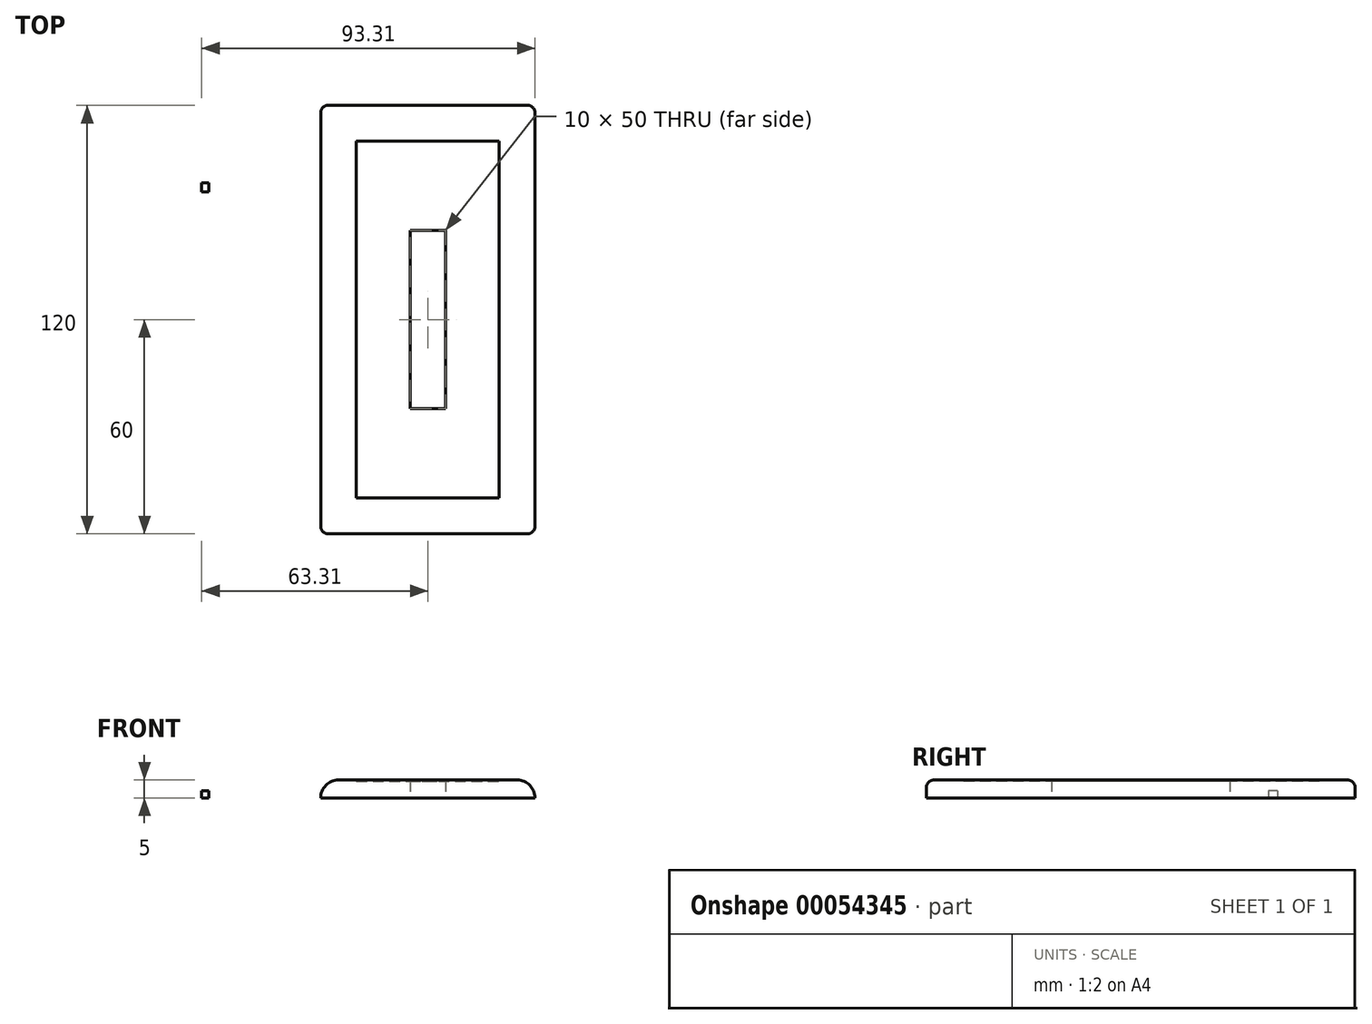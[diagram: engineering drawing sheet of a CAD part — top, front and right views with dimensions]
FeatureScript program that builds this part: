
annotation { "Feature Type Name" : "Feature", "Feature Type Description" : "" }
export const myFeature = defineFeature(function(context is Context, id is Id, definition is map)
    precondition{}
    {
        {
            var Q0;
            Q0=qCreatedBy(makeId("Top.planeOp"),FACE);
            var sketch = newSketch(context, id + "F0", { "sketchPlane" : qUnion([Q0])});
            skLineSegment(sketch, "E0.rect.bottom", {"start": v(-30, 60) * mm, "end": v(30, 60) * mm});
            skLineSegment(sketch, "E0.rect.top", {"start": v(-30, -60) * mm, "end": v(30, -60) * mm});
            skLineSegment(sketch, "E0.rect.left", {"start": v(-30, 60) * mm, "end": v(-30, -60) * mm});
            skLineSegment(sketch, "E0.rect.right", {"start": v(30, 60) * mm, "end": v(30, -60) * mm});
            skPoint(sketch, "E0.rect.middle", {"position": v(0, 0) * mm});
            skLineSegment(sketch, "E1.rect.bottom", {"start": v(-20, 50) * mm, "end": v(20, 50) * mm});
            skLineSegment(sketch, "E1.rect.top", {"start": v(-20, -50) * mm, "end": v(20, -50) * mm});
            skLineSegment(sketch, "E1.rect.left", {"start": v(-20, 50) * mm, "end": v(-20, -50) * mm});
            skLineSegment(sketch, "E1.rect.right", {"start": v(20, 50) * mm, "end": v(20, -50) * mm});
            skLineSegment(sketch, "E2.rect.bottom", {"start": v(-5, 25) * mm, "end": v(5, 25) * mm});
            skLineSegment(sketch, "E2.rect.top", {"start": v(-5, -25) * mm, "end": v(5, -25) * mm});
            skLineSegment(sketch, "E2.rect.left", {"start": v(-5, 25) * mm, "end": v(-5, -25) * mm});
            skLineSegment(sketch, "E2.rect.right", {"start": v(5, 25) * mm, "end": v(5, -25) * mm});
            skSolve(sketch);
        }
        {
            var Q0;
            Q0=makeQuery(id+"F0.imprint","IMPRINT",FACE,{"disambiguationData":[TD([[makeQuery(id+"F0.imprint","IMPRINT",EDGE,{"derivedFrom":sQuery(id+"F0.wireOp",EDGE,"E0.rect.bottom")}),-1.0]])]});
            extrude(context, id + "F1", {"entities" : qUnion([Q0]), "depth" : 5 * mm});
        }
        {
            var Q0;
            Q0=makeQuery(id+"F1.opExtrude","CAP_EDGE",EDGE,{"disambiguationData":[OSD([sQuery(id+"F0.wireOp",EDGE,"E0.rect.left")])],"isStart":false});
            var Q1;
            Q1=makeQuery(id+"F1.opExtrude","CAP_EDGE",EDGE,{"disambiguationData":[OSD([sQuery(id+"F0.wireOp",EDGE,"E0.rect.right")])],"isStart":false});
            fillet(context, id + "F2", {"entities" : qUnion([Q0, Q1]), "radius" : 5 * mm, "tangentPropagation" : true, "allowEdgeOverflow" : false});
        }
        {
            var Q0;
            Q0=makeQuery(id+"F1.opExtrude","CAP_EDGE",EDGE,{"disambiguationData":[OSD([sQuery(id+"F0.wireOp",EDGE,"E0.rect.bottom")])],"isStart":false});
            var Q1;
            Q1=makeQuery(id+"F1.opExtrude","CAP_EDGE",EDGE,{"disambiguationData":[OSD([sQuery(id+"F0.wireOp",EDGE,"E0.rect.top")])],"isStart":false});
            fillet(context, id + "F3", {"entities" : qUnion([Q0, Q1]), "radius" : 2 * mm, "tangentPropagation" : true, "allowEdgeOverflow" : false});
        }
        {
            var Q0;
            Q0=makeQuery(id+"F0.imprint","IMPRINT",FACE,{"disambiguationData":[TD([[makeQuery(id+"F0.imprint","IMPRINT",EDGE,{"derivedFrom":sQuery(id+"F0.wireOp",EDGE,"E1.rect.bottom")}),-1.0]])]});
            extrude(context, id + "F4", {"entities" : qUnion([Q0]), "operationType" : NewBodyOperationType.ADD, "depth" : 4.7 * mm});
        }
        {
            var Q0;
            Q0=qCreatedBy(makeId("Top.planeOp"),FACE);
            var sketch = newSketch(context, id + "F5", { "sketchPlane" : qUnion([Q0])});
            skLineSegment(sketch, "E3.bottom", {"start": v(-63.3, 38.26) * mm, "end": v(-61.3, 38.26) * mm});
            skLineSegment(sketch, "E3.top", {"start": v(-63.3, 35.76) * mm, "end": v(-61.3, 35.76) * mm});
            skLineSegment(sketch, "E3.left", {"start": v(-63.3, 38.26) * mm, "end": v(-63.3, 35.76) * mm});
            skLineSegment(sketch, "E3.right", {"start": v(-61.3, 38.26) * mm, "end": v(-61.3, 35.76) * mm});
            skSolve(sketch);
        }
        {
            var Q0;
            Q0=makeQuery(id+"F5.imprint","IMPRINT",FACE,{"disambiguationData":[TD([[makeQuery(id+"F5.imprint","IMPRINT",EDGE,{"derivedFrom":sQuery(id+"F5.wireOp",EDGE,"E3.bottom")}),-1.0]])]});
            extrude(context, id + "F6", {"entities" : qUnion([Q0]), "depth" : 2 * mm});
        }
    });
